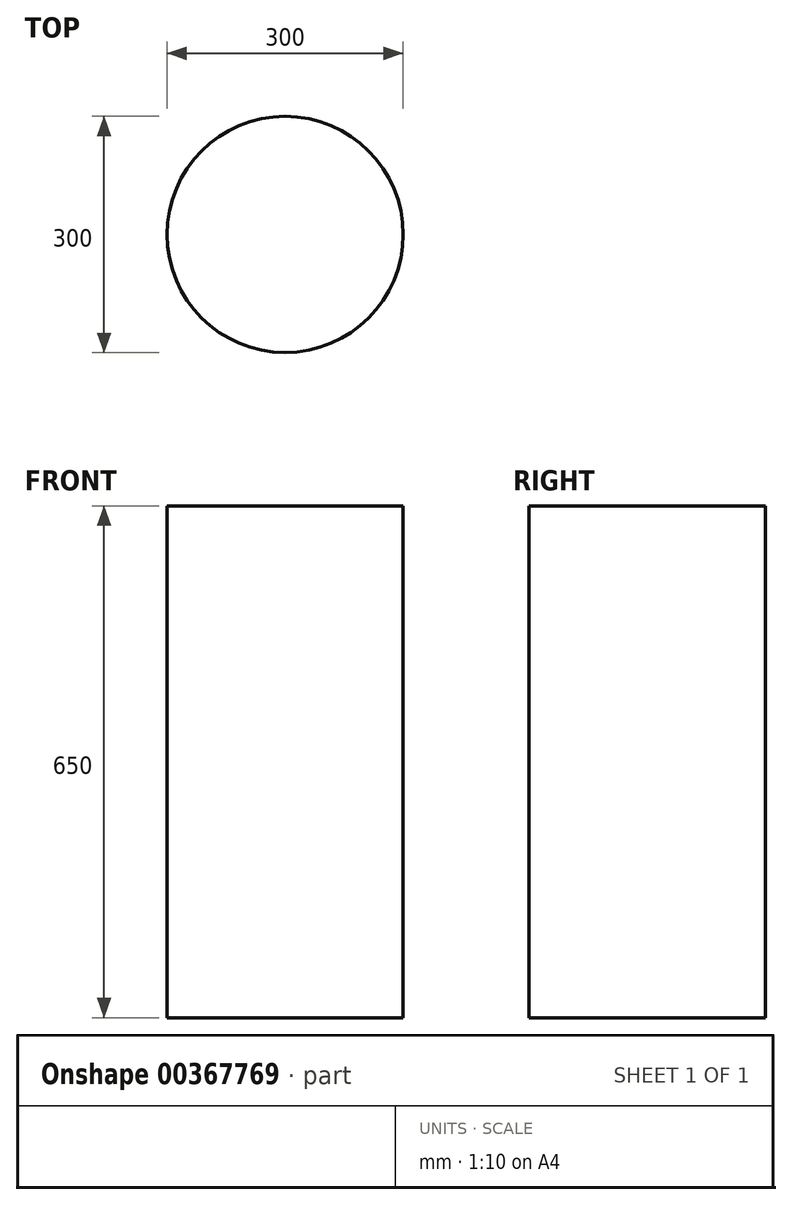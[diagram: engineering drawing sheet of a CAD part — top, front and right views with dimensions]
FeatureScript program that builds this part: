
annotation { "Feature Type Name" : "Feature", "Feature Type Description" : "" }
export const myFeature = defineFeature(function(context is Context, id is Id, definition is map)
    precondition{}
    {
        {
            var Q0;
            Q0=qCreatedBy(makeId("Top.planeOp"),FACE);
            var sketch = newSketch(context, id + "F0", { "sketchPlane" : qUnion([Q0])});
            skCircle(sketch, "E0", {"center": v(0, 0) * mm, "radius": 150 * mm});
            skSolve(sketch);
        }
        {
            var Q0;
            Q0=makeQuery(id+"F0.imprint","IMPRINT",FACE,{"disambiguationData":[TD([[makeQuery(id+"F0.imprint","IMPRINT",EDGE,{"derivedFrom":sQuery(id+"F0.wireOp",EDGE,"E0")}),1.0]])]});
            extrude(context, id + "F1", {"entities" : qUnion([Q0]), "depth" : 650 * mm});
        }
    });
